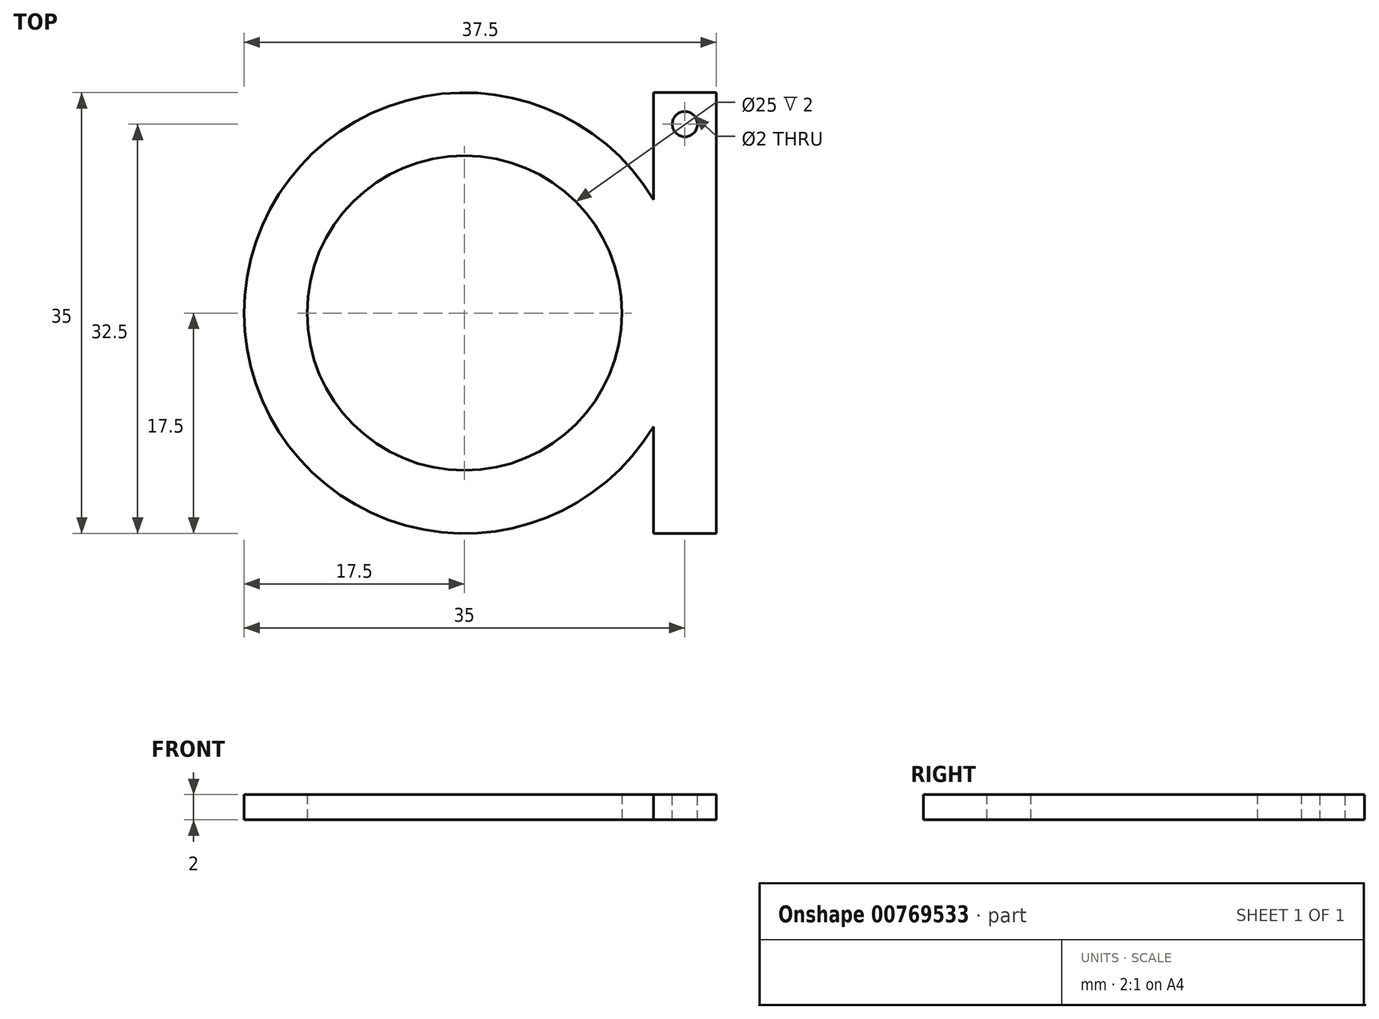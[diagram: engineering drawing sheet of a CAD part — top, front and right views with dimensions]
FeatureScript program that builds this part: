
annotation { "Feature Type Name" : "Feature", "Feature Type Description" : "" }
export const myFeature = defineFeature(function(context is Context, id is Id, definition is map)
    precondition{}
    {
        {
            var Q0;
            Q0=qCreatedBy(makeId("Top.planeOp"),FACE);
            var sketch = newSketch(context, id + "F0", { "sketchPlane" : qUnion([Q0])});
            skCircle(sketch, "E0", {"center": v(0, 0) * mm, "radius": 17.5 * mm});
            skCircle(sketch, "E1", {"center": v(0, 0) * mm, "radius": 12.5 * mm});
            skLineSegment(sketch, "E2.bottom", {"start": v(15, 17.5) * mm, "end": v(20, 17.5) * mm});
            skLineSegment(sketch, "E2.top", {"start": v(15, -17.5) * mm, "end": v(20, -17.5) * mm});
            skLineSegment(sketch, "E2.left", {"start": v(15, 17.5) * mm, "end": v(15, -17.5) * mm});
            skLineSegment(sketch, "E2.right", {"start": v(20, 17.5) * mm, "end": v(20, -17.5) * mm});
            skSolve(sketch);
        }
        {
            var Q0;
            Q0=makeQuery(id+"F0.imprint","IMPRINT",FACE,{"disambiguationData":[TD([[makeQuery(id+"F0.imprint","IMPRINT",EDGE,{"derivedFrom":sQuery(id+"F0.wireOp",EDGE,"E1")}),-1.0]])]});
            var Q1;
            {var subQ0=sQuery(id+"F0.wireOp",EDGE,"E2.left");var subQ1=sQuery(id+"F0.wireOp",EDGE,"E0");var subQ2=makeQuery(id+"F0.imprint","INTERSECT",VERTEX,{"disambiguationData":[OD(0.0)],"derivedFrom":[subQ1,subQ0]});Q1=makeQuery(id+"F0.imprint","IMPRINT",FACE,{"disambiguationData":[TD([[makeQuery(id+"F0.imprint","IMPRINT",EDGE,{"disambiguationData":[TD([[subQ2,1.0]])],"derivedFrom":subQ1}),1.0]])]});}
            var Q2;
            {var subQ1=sQuery(id+"F0.wireOp",EDGE,"E2.bottom");Q2=makeQuery(id+"F0.imprint","IMPRINT",FACE,{"disambiguationData":[TD([[makeQuery(id+"F0.imprint","IMPRINT",EDGE,{"derivedFrom":subQ1}),-1.0]])]});}
            extrude(context, id + "F1", {"entities" : qUnion([Q0, Q1, Q2]), "depth" : 2 * mm, "offsetDistance" : 25 * mm});
        }
        {
            var Q0;
            Q0=makeQuery(id+"F1.opExtrude","CAP_FACE",FACE,{"disambiguationData":[OSD([sQuery(id+"F0.wireOp",EDGE,"E0"),sQuery(id+"F0.wireOp",EDGE,"E1"),sQuery(id+"F0.wireOp",EDGE,"E2.bottom"),sQuery(id+"F0.wireOp",EDGE,"E2.top"),sQuery(id+"F0.wireOp",EDGE,"E2.left"),sQuery(id+"F0.wireOp",EDGE,"E2.right")])],"isStart":false});
            var sketch = newSketch(context, id + "F2", { "sketchPlane" : qUnion([Q0])});
            skCircle(sketch, "E3", {"center": v(17.5, 15) * mm, "radius": 1 * mm});
            skSolve(sketch);
        }
        {
            var Q0;
            Q0=makeQuery(id+"F2.imprint","IMPRINT",FACE,{"disambiguationData":[TD([[makeQuery(id+"F2.imprint","IMPRINT",EDGE,{"derivedFrom":sQuery(id+"F2.wireOp",EDGE,"E3")}),1.0]])]});
            extrude(context, id + "F3", {"entities" : qUnion([Q0]), "operationType" : NewBodyOperationType.REMOVE, "oppositeDirection" : true, "depth" : 2 * mm, "offsetDistance" : 25 * mm});
        }
    });
